# Revit family: Sink-DXV-Hillside-D20066236.415
name_source: partatom
category: Plumbing Fixtures
revit_build: Autodesk Revit 2014 (Build: 20130308_1515(x64)
units: mm (PartAtom-declared; Revit-internal decimal feet)

## types (1)
- D20066236.415
    ADA Compliant = Yes
    Assembly Code = D2010410
    Basin Shape = Rectangular
    Bowl Length = 15"
    Bowl Width = 32 1/2"
    CW Connection = Yes
    CWFU = 3
    Cold Water Connection Diameter = 1/2"
    Cold Water Connection Radius = 1/4"
    Cold Water Connection Width = 4"
    Default Elevation = 34"
    Description = Hillside 36'' Apron Kitchen
    Finish = Fine Fire Clay-DXV-415-Canvas White
    HW Connection = Yes
    HWFU = 3
    Height = 9 5/8"
    Hot Water Connection Diameter = 1"
    Hot Water Connection Radius = 1/4"
    Hot Water Connection Width = 4"
    Installation Type = Dual Mount
    Length = 18 3/16"
    Manufacturer = DXV
    Material = Fine Fire Clay-DXV-415-Canvas White
    Model = D20066236.415
    Price = Prices may vary. Please consult Manufacturer Representative for most up-to-date price list.
    Product Documentation Link = https://dxv01.blob.core.windows.net
    Product Page URL = https://www.dxv.com
    Topmount Installation = Yes
    Type Comments = 33" (838mm) cabinet required
    URL = https://www.dxv.com
    Undermount Installation = No
    Vent Connection = No
    WFU = 4
    Warranty Information = 5 Year Limited Warranty, 1 Year Warranty on Accessories
    Waste Connection = Yes
    Waste Connection Diameter = 1 1/2"
    Waste Connection Offset = 6 1/4"
    Waste Connection Radius = 3/4"
    Waste Connection Width = 5 7/8"
    Width = 35 5/8"

## geometry (parser evidence)
native form markers: Sweep x1
no freeform markers — native parametric forms only
